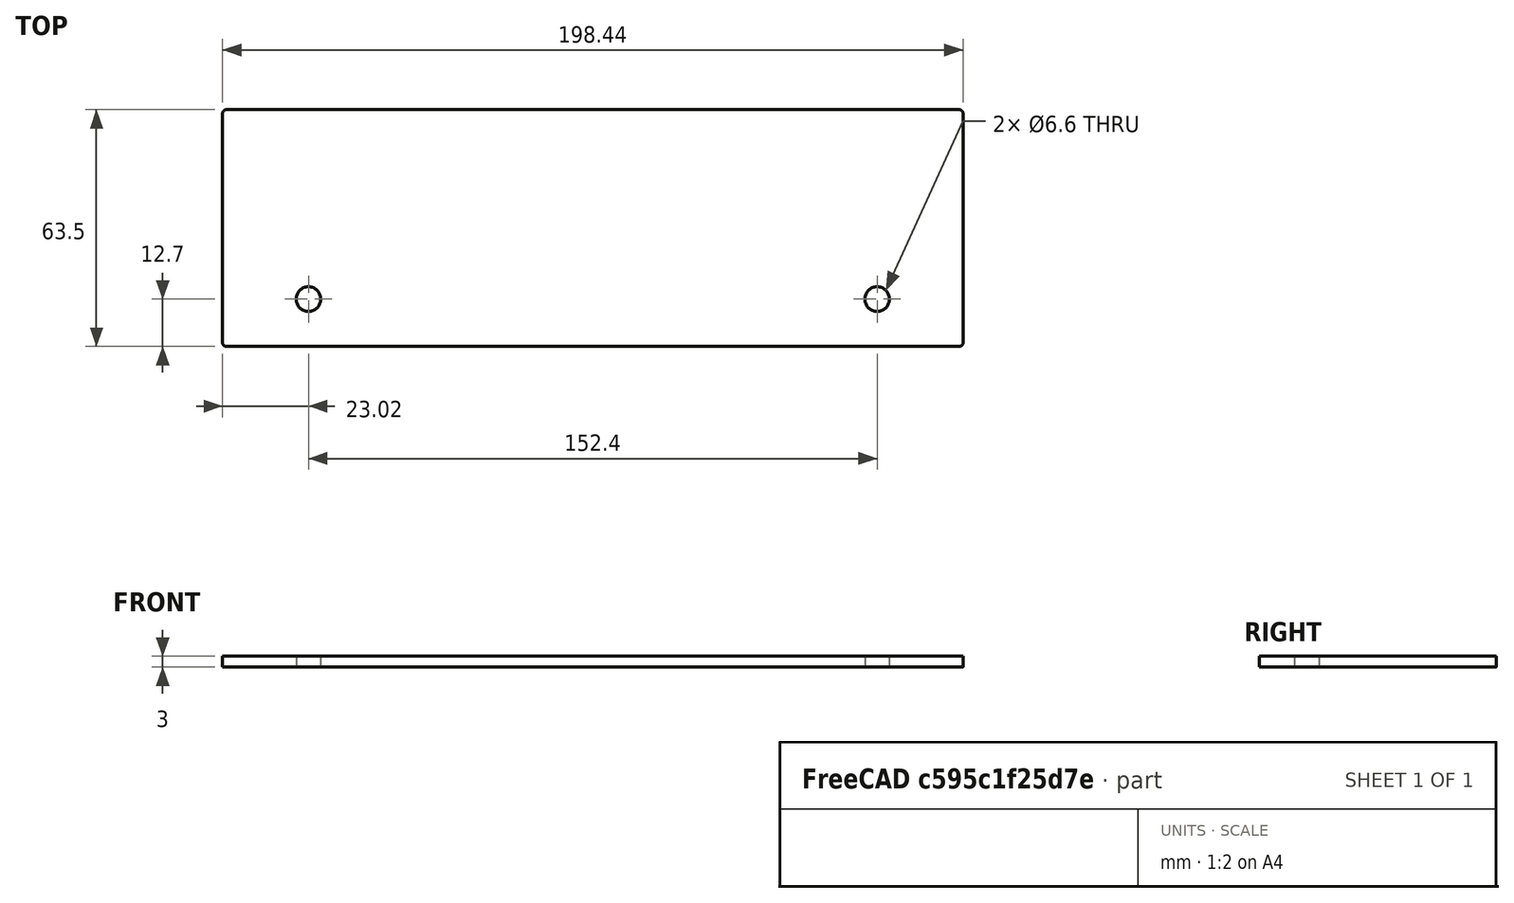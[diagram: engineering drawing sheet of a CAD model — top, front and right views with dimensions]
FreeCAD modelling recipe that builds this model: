
FCSTD DOCUMENT  (FreeCAD 0.20R29603 (Git))
Label: left_wall_test_rig
License: All rights reserved
LicenseURL: http://en.wikipedia.org/wiki/All_rights_reserved
objects: Sketcher::SketchObject×2, Spreadsheet::Sheet×1, PartDesign::Pad×1, PartDesign::Body×1, Part::Part2DObjectPython×1
note: 6 computed .brp shape members not serialized (recipe doc carries the construction recipe); baked Part::Feature solids carry a one-line shape summary decoded from their .brp

FEATURE [Sketcher::SketchObject] Sketch
  FullyConstrained = true
  MapMode = 5
  Support = -> [XY_Plane]
  expr: Constraints[19] = Spreadsheet.FilletRadius
  expr: Constraints[21] = Spreadsheet.Height
  expr: Constraints[22] = Spreadsheet.Length
  expr: Constraints[28] = Spreadsheet.MountHoleSpacing
  expr: Constraints[29] = Spreadsheet.MountHoleDistanceFromBottom
  expr: Constraints[31] = Spreadsheet.MountHoleDiameter
  sketch-geometry (14):
    g0: ArcOfCircle CenterX=-98.2188 CenterY=30.75 CenterZ=0 NormalX=0 NormalY=0 NormalZ=1 AngleXU=0 Radius=1 StartAngle=1.5708 EndAngle=3.14159
    g1: LineSegment StartX=-98.2188 StartY=31.75 StartZ=0 EndX=98.2188 EndY=31.75 EndZ=0
    g2: ArcOfCircle CenterX=98.2188 CenterY=30.75 CenterZ=0 NormalX=0 NormalY=0 NormalZ=1 AngleXU=0 Radius=1 StartAngle=9e-16 EndAngle=1.5708
    g3: LineSegment StartX=99.2188 StartY=30.75 StartZ=0 EndX=99.2188 EndY=-30.75 EndZ=0
    g4: ArcOfCircle CenterX=98.2188 CenterY=-30.75 CenterZ=0 NormalX=0 NormalY=0 NormalZ=1 AngleXU=0 Radius=1 StartAngle=4.71239 EndAngle=6.28319
    g5: LineSegment StartX=98.2188 StartY=-31.75 StartZ=0 EndX=-98.2188 EndY=-31.75 EndZ=0
    g6: ArcOfCircle CenterX=-98.2188 CenterY=-30.75 CenterZ=0 NormalX=0 NormalY=0 NormalZ=1 AngleXU=0 Radius=1 StartAngle=3.14159 EndAngle=4.71239
    g7: LineSegment StartX=-99.2188 StartY=-30.75 StartZ=0 EndX=-99.2188 EndY=30.75 EndZ=0
    g8: GeomPoint X=-99.2188 Y=31.75 Z=0
    g9: GeomPoint X=99.2188 Y=-31.75 Z=0
    g10: LineSegment StartX=-76.2 StartY=-19.05 StartZ=0 EndX=76.2 EndY=-19.05 EndZ=0
    g11: LineSegment StartX=0 StartY=-31.75 StartZ=0 EndX=0 EndY=-19.05 EndZ=0
    g12: Circle CenterX=-76.2 CenterY=-19.05 CenterZ=0 NormalX=0 NormalY=0 NormalZ=1 AngleXU=0 Radius=3.302
    g13: Circle CenterX=76.2 CenterY=-19.05 CenterZ=0 NormalX=0 NormalY=0 NormalZ=1 AngleXU=0 Radius=3.302
  constraints (34):
    c: Tangent(g0,g1) = 1.5708
    c: Tangent(g1,g2) = 1.5708
    c: Tangent(g2,g3) = 1.5708
    c: Tangent(g3,g4) = 1.5708
    c: Tangent(g4,g5) = 1.5708
    c: Tangent(g5,g6) = 1.5708
    c: Tangent(g6,g7) = 1.5708
    c: Tangent(g7,g0) = 1.5708
    c: Horizontal(g1)
    c: Horizontal(g5)
    c: Vertical(g3)
    c: Vertical(g7)
    c: Equal(g0,g2)
    c: Equal(g2,g4)
    c: Equal(g4,g6)
    c: PointOnObject(g8,g1)
    c: PointOnObject(g8,g7)
    c: PointOnObject(g9,g3)
    c: PointOnObject(g9,g5)
    c: Radius(g2) = 1
    c: Symmetric(g8,g9,g-1)
    c: DistanceY(g4,g1) = 63.5
    c: DistanceX(g0,g2) = 198.438
    c: Horizontal(g10)
    c: Vertical(g11)
    c: PointOnObject(g11,g5)
    c: PointOnObject(g11,g-2)
    c: Symmetric(g10,g10,g11)
    c: DistanceX(g10,g10) = 152.4
    c: DistanceY(g11,g11) = 12.7
    c: Coincident(g13,g10)
    c: Diameter(g13) = 6.604
    c: Equal(g12,g13)
    c: Coincident(g12,g10)
FEATURE [Spreadsheet::Sheet] Spreadsheet
  cells = A2=Parameters; A3=Height; B3(Height)==2.5in; A4=Length; B4(Length)==7.8125in; A5=Thickness; B5(Thickness)==3mm; A6=FilletRadius; B6(FilletRadius)==1mm; A7=MountHoleDiameter; B7(MountHoleDiameter)==0.26in; A8=MountHoleDistanceFromBottom; B8(MountHoleDistanceFromBottom)==0.5in; A9=MountHoleSpacing; B9(MountHoleSpacing)==6in
FEATURE [PartDesign::Pad] Pad
  Direction = (0,0,1)
  Length = 3
  Length2 = 10
  Profile = -> Sketch
  ReferenceAxis = -> Sketch [N_Axis]
  Type = 0
  expr: Length = Spreadsheet.Thickness
FEATURE [PartDesign::Body] Body
  Group = -> [Sketch,Pad]
  Origin = -> Origin
  Tip = -> Pad
FEATURE [Part::Part2DObjectPython] Shape2DView  # Draft 2D object (typed FeaturePython)
  AutoUpdate = true
  Base = -> Pad
  Clip = false
  FaceNumbers = [11]
  FuseArch = false
  HiddenLines = false
  InPlace = true
  OnlySolids = false
  Projection = (0,0,1)
  ProjectionMode = 0
  SegmentLength = 0.05
  Tessellation = false
  VisibleOnly = false
FEATURE [Sketcher::SketchObject] Sketch001
  FullyConstrained = false
  sketch-geometry (10):
    g0: ArcOfCircle CenterX=-98.2188 CenterY=30.75 CenterZ=0 NormalX=0 NormalY=0 NormalZ=1 AngleXU=0 Radius=1 StartAngle=1.5708 EndAngle=3.14159
    g1: LineSegment StartX=-99.2188 StartY=-30.75 StartZ=0 EndX=-99.2188 EndY=30.75 EndZ=0
    g2: ArcOfCircle CenterX=-98.2188 CenterY=-30.75 CenterZ=0 NormalX=0 NormalY=0 NormalZ=1 AngleXU=0 Radius=1 StartAngle=3.14159 EndAngle=4.71239
    g3: LineSegment StartX=98.2188 StartY=-31.75 StartZ=0 EndX=-98.2188 EndY=-31.75 EndZ=0
    g4: ArcOfCircle CenterX=98.2188 CenterY=-30.75 CenterZ=0 NormalX=0 NormalY=0 NormalZ=1 AngleXU=0 Radius=1 StartAngle=4.71239 EndAngle=6.28319
    g5: LineSegment StartX=99.2188 StartY=30.75 StartZ=0 EndX=99.2188 EndY=-30.75 EndZ=0
    g6: ArcOfCircle CenterX=98.2188 CenterY=30.75 CenterZ=0 NormalX=0 NormalY=0 NormalZ=1 AngleXU=0 Radius=1 StartAngle=1e-15 EndAngle=1.5708
    g7: LineSegment StartX=-98.2188 StartY=31.75 StartZ=0 EndX=98.2188 EndY=31.75 EndZ=0
    g8: Circle CenterX=76.2 CenterY=-19.05 CenterZ=0 NormalX=0 NormalY=0 NormalZ=1 AngleXU=0 Radius=3.302
    g9: Circle CenterX=-76.2 CenterY=-19.05 CenterZ=0 NormalX=0 NormalY=0 NormalZ=1 AngleXU=0 Radius=3.302
